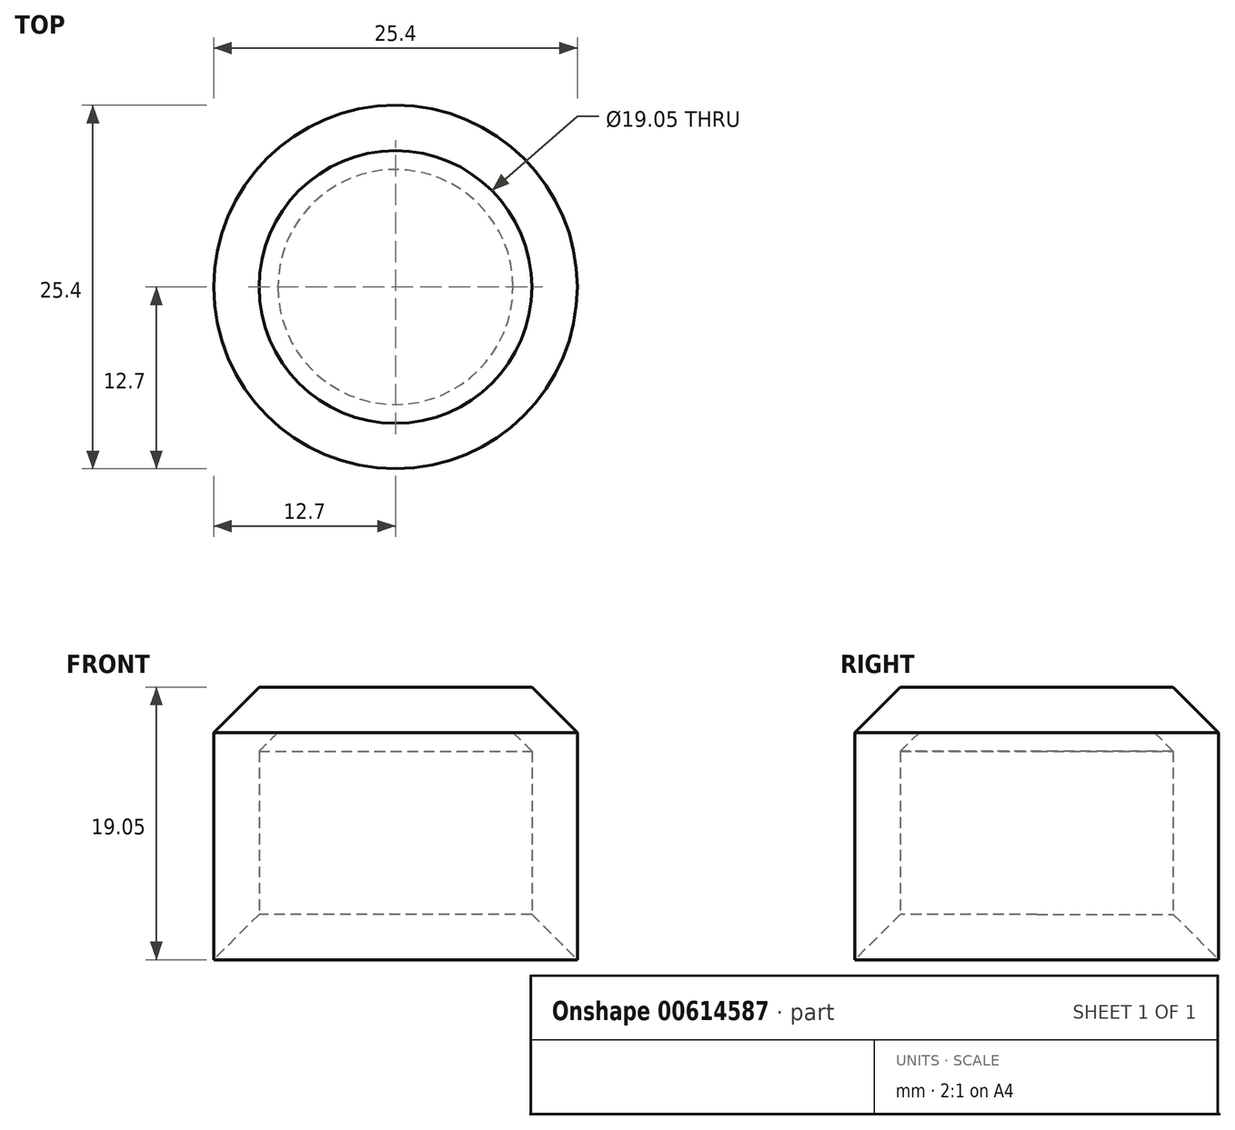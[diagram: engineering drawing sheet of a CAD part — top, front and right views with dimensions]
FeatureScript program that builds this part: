
annotation { "Feature Type Name" : "Feature", "Feature Type Description" : "" }
export const myFeature = defineFeature(function(context is Context, id is Id, definition is map)
    precondition{}
    {
        {
            var Q0;
            Q0=qCreatedBy(makeId("Top.planeOp"),FACE);
            var sketch = newSketch(context, id + "F0", { "sketchPlane" : qUnion([Q0])});
            skCircle(sketch, "E0", {"center": v(0, 0) * mm, "radius": 12.7 * mm});
            skSolve(sketch);
        }
        {
            var Q0;
            Q0=makeQuery(id+"F0.imprint","IMPRINT",FACE,{"disambiguationData":[TD([[makeQuery(id+"F0.imprint","IMPRINT",EDGE,{"derivedFrom":sQuery(id+"F0.wireOp",EDGE,"E0")}),1.0]])]});
            extrude(context, id + "F1", {"entities" : qUnion([Q0]), "depth" : 19.05 * mm, "offsetDistance" : 25.4 * mm});
        }
        {
            var Q0;
            Q0=makeQuery(id+"F1.opExtrude","CAP_EDGE",EDGE,{"disambiguationData":[OSD([sQuery(id+"F0.wireOp",EDGE,"E0")])],"isStart":false});
            chamfer(context, id + "F2", {"entities" : qUnion([Q0]), "width" : 3.17 * mm, "tangentPropagation" : true});
        }
        {
            var Q0;
            Q0=makeQuery(id+"F1.opExtrude","CAP_FACE",FACE,{"disambiguationData":[OSD([sQuery(id+"F0.wireOp",EDGE,"E0")])],"isStart":true});
            shell(context, id + "F3", {"entities" : qUnion([Q0]), "thickness" : 3.17 * mm});
        }
        {
            var Q0;
            {var subQ0=sQuery(id+"F0.wireOp",EDGE,"E0");Q0=makeQuery(id+"F3.opShell","OFFSET_EDGE",EDGE,{"disambiguationData":[OSD([subQ0]),TDD([makeQuery(id+"F1.opExtrude","CAP_EDGE",EDGE,{"disambiguationData":[OSD([subQ0])],"isStart":true})])]});}
            chamfer(context, id + "F4", {"entities" : qUnion([Q0]), "width" : 3.17 * mm, "tangentPropagation" : true});
        }
    });
